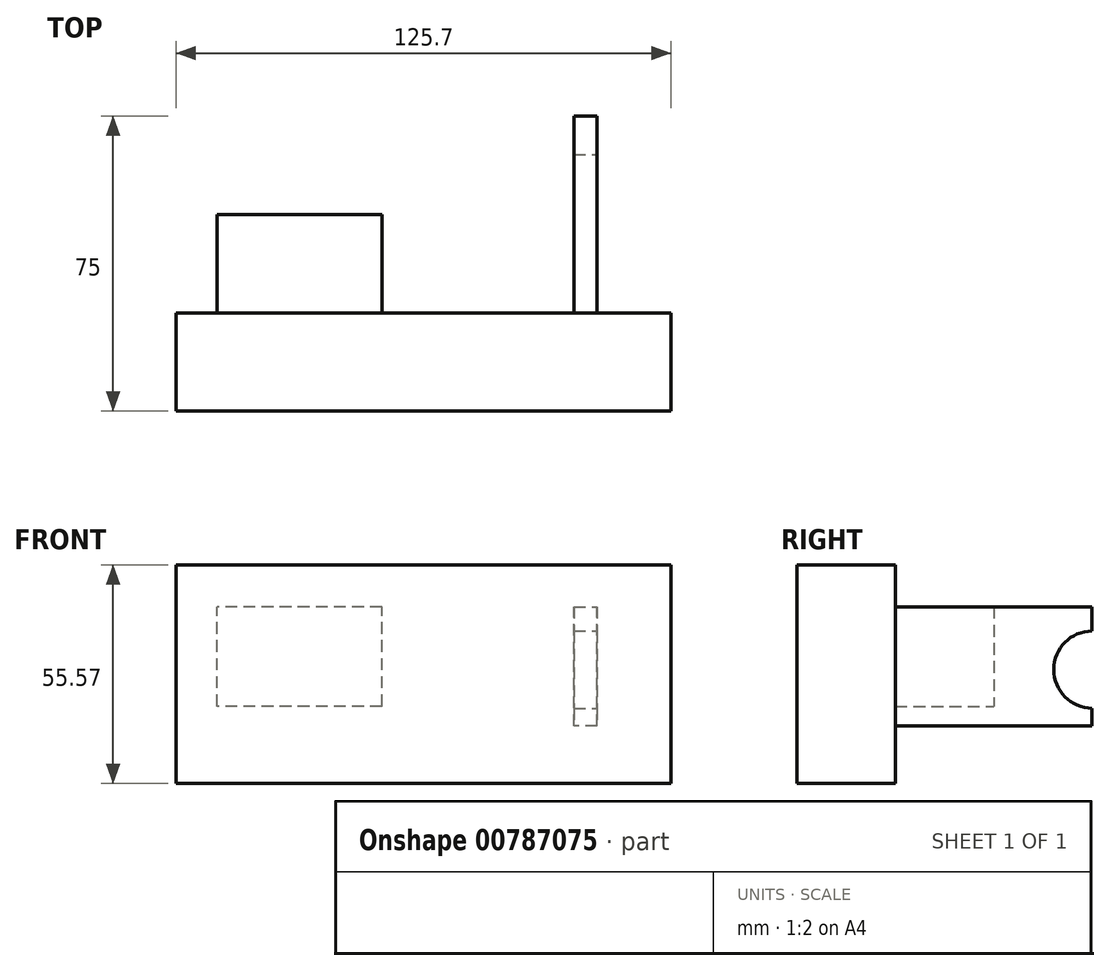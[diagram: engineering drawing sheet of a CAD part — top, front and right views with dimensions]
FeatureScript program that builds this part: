
annotation { "Feature Type Name" : "Feature", "Feature Type Description" : "" }
export const myFeature = defineFeature(function(context is Context, id is Id, definition is map)
    precondition{}
    {
        {
            var Q0;
            Q0=qCreatedBy(makeId("Front.planeOp"),FACE);
            var sketch = newSketch(context, id + "F0", { "sketchPlane" : qUnion([Q0])});
            skLineSegment(sketch, "E0.bottom", {"start": v(-66.12, 26.3) * mm, "end": v(59.58, 26.3) * mm});
            skLineSegment(sketch, "E0.top", {"start": v(-66.12, -29.27) * mm, "end": v(59.58, -29.27) * mm});
            skLineSegment(sketch, "E0.left", {"start": v(-66.12, 26.3) * mm, "end": v(-66.12, -29.27) * mm});
            skLineSegment(sketch, "E0.right", {"start": v(59.58, 26.3) * mm, "end": v(59.58, -29.27) * mm});
            skLineSegment(sketch, "E1.bottom", {"start": v(-55.72, 15.6) * mm, "end": v(-13.82, 15.6) * mm});
            skLineSegment(sketch, "E1.top", {"start": v(-55.72, -9.66) * mm, "end": v(-13.82, -9.66) * mm});
            skLineSegment(sketch, "E1.left", {"start": v(-55.72, 15.6) * mm, "end": v(-55.72, -9.66) * mm});
            skLineSegment(sketch, "E1.right", {"start": v(-13.82, 15.6) * mm, "end": v(-13.82, -9.66) * mm});
            skLineSegment(sketch, "E2.bottom", {"start": v(34.92, 15.6) * mm, "end": v(40.86, 15.6) * mm});
            skLineSegment(sketch, "E2.top", {"start": v(34.92, -14.7) * mm, "end": v(40.86, -14.7) * mm});
            skLineSegment(sketch, "E2.left", {"start": v(34.92, 15.6) * mm, "end": v(34.92, -14.7) * mm});
            skLineSegment(sketch, "E2.right", {"start": v(40.86, 15.6) * mm, "end": v(40.86, -14.7) * mm});
            skSolve(sketch);
        }
        {
            var Q0;
            Q0=makeQuery(id+"F0.imprint","IMPRINT",FACE,{"disambiguationData":[TD([[makeQuery(id+"F0.imprint","IMPRINT",EDGE,{"derivedFrom":sQuery(id+"F0.wireOp",EDGE,"E1.bottom")}),-1.0]])]});
            var Q1;
            Q1=makeQuery(id+"F0.imprint","IMPRINT",FACE,{"disambiguationData":[TD([[makeQuery(id+"F0.imprint","IMPRINT",EDGE,{"derivedFrom":sQuery(id+"F0.wireOp",EDGE,"E2.bottom")}),-1.0]])]});
            var Q2;
            Q2=makeQuery(id+"F0.imprint","IMPRINT",FACE,{"disambiguationData":[TD([[makeQuery(id+"F0.imprint","IMPRINT",EDGE,{"derivedFrom":sQuery(id+"F0.wireOp",EDGE,"E0.bottom")}),-1.0]])]});
            extrude(context, id + "F1", {"entities" : qUnion([Q0, Q1, Q2]), "depth" : 25 * mm, "offsetDistance" : 25 * mm});
        }
        {
            var Q0;
            Q0=makeQuery(id+"F0.imprint","IMPRINT",FACE,{"disambiguationData":[TD([[makeQuery(id+"F0.imprint","IMPRINT",EDGE,{"derivedFrom":sQuery(id+"F0.wireOp",EDGE,"E1.bottom")}),-1.0]])]});
            extrude(context, id + "F2", {"entities" : qUnion([Q0]), "operationType" : NewBodyOperationType.ADD, "depth" : 25 * mm, "offsetDistance" : 25 * mm, "hasSecondDirection" : true, "secondDirectionOppositeDirection" : true, "secondDirectionDepth" : 25 * mm});
        }
        {
            var Q0;
            Q0=makeQuery(id+"F0.imprint","IMPRINT",FACE,{"disambiguationData":[TD([[makeQuery(id+"F0.imprint","IMPRINT",EDGE,{"derivedFrom":sQuery(id+"F0.wireOp",EDGE,"E2.bottom")}),-1.0]])]});
            extrude(context, id + "F3", {"entities" : qUnion([Q0]), "operationType" : NewBodyOperationType.ADD, "depth" : 25 * mm, "offsetDistance" : 25 * mm, "hasSecondDirection" : true, "secondDirectionOppositeDirection" : true, "secondDirectionDepth" : 50 * mm});
        }
        {
            var Q0;
            Q0=makeQuery(id+"F3.opExtrude","SWEPT_FACE",FACE,{"disambiguationData":[OSD([sQuery(id+"F0.wireOp",EDGE,"E2.right")])]});
            var sketch = newSketch(context, id + "F4", { "sketchPlane" : qUnion([Q0])});
            skArc(sketch, "E3", {"start": v(50, 9.47) * mm, "mid": v(40.25, -0.34) * mm, "end": v(50, -10.15) * mm});
            skSolve(sketch);
        }
        {
            var Q0;
            {var subQ0=sQuery(id+"F4.wireOp",EDGE,"E3");Q0=makeQuery(id+"F4.imprint","IMPRINT",FACE,{"disambiguationData":[TD([[makeQuery(id+"F4.imprint","IMPRINT",EDGE,{"derivedFrom":subQ0}),1.0]])]});}
            extrude(context, id + "F5", {"entities" : qUnion([Q0]), "operationType" : NewBodyOperationType.REMOVE, "endBound" : BoundingType.THROUGH_ALL, "oppositeDirection" : true, "depth" : 25 * mm, "offsetDistance" : 25 * mm});
        }
    });
